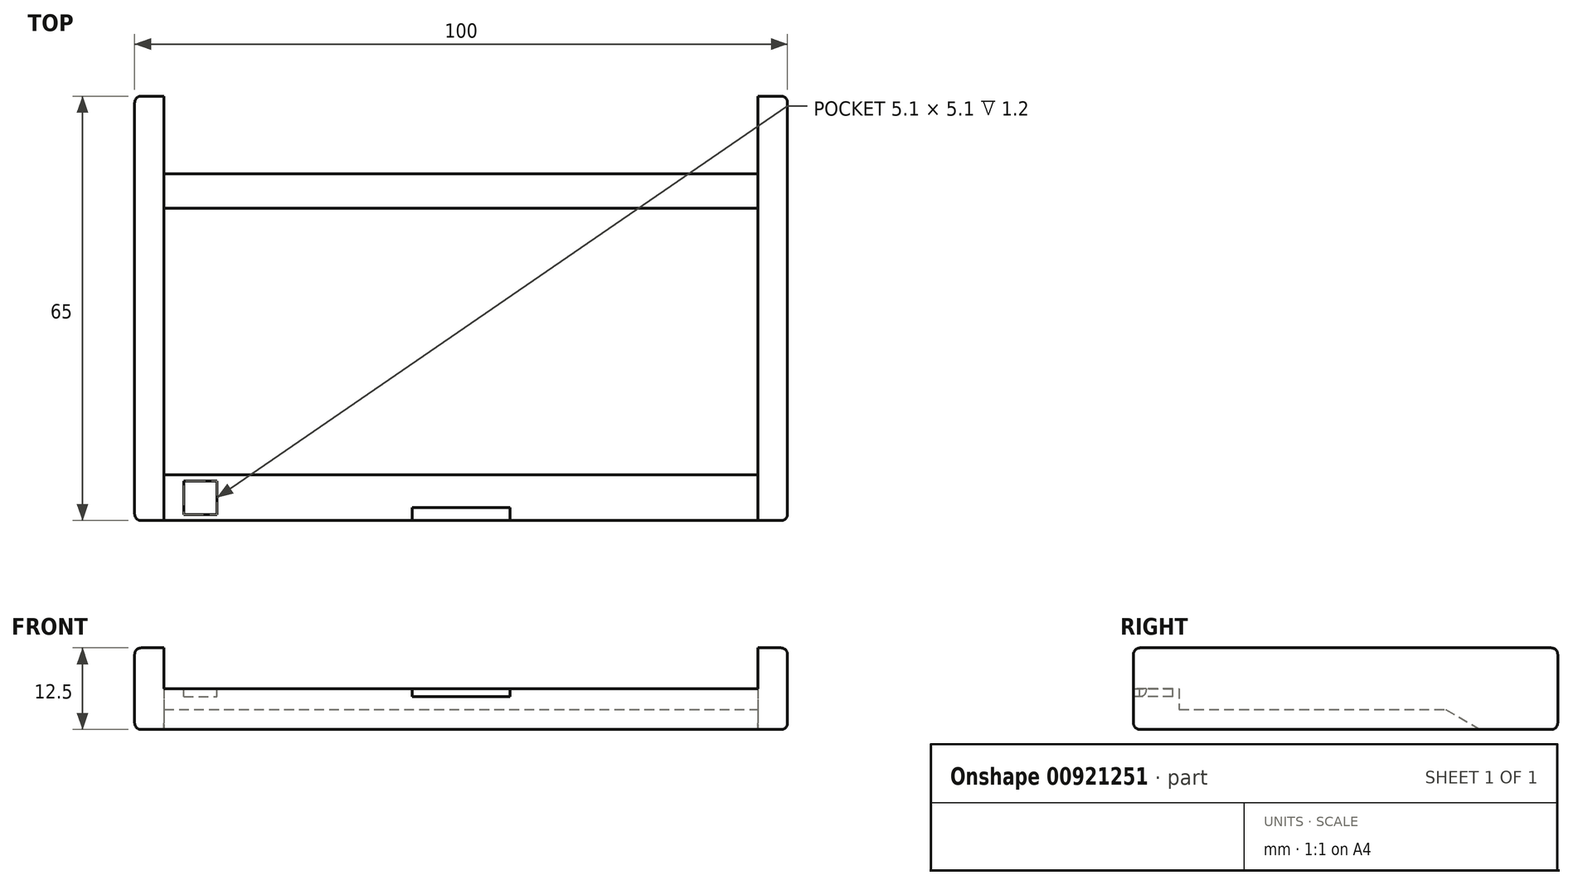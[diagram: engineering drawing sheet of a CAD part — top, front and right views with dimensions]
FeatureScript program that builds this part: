
annotation { "Feature Type Name" : "Feature", "Feature Type Description" : "" }
export const myFeature = defineFeature(function(context is Context, id is Id, definition is map)
    precondition{}
    {
        {
            var Q0;
            Q0=qCreatedBy(makeId("Right.planeOp"),FACE);
            var sketch = newSketch(context, id + "F0", { "sketchPlane" : qUnion([Q0])});
            skLineSegment(sketch, "E0.bottom", {"start": v(-32.5, 6.25) * mm, "end": v(32.5, 6.25) * mm});
            skLineSegment(sketch, "E0.top", {"start": v(-32.5, -6.25) * mm, "end": v(32.5, -6.25) * mm});
            skLineSegment(sketch, "E0.left", {"start": v(-32.5, 6.25) * mm, "end": v(-32.5, -6.25) * mm});
            skLineSegment(sketch, "E0.right", {"start": v(32.5, 6.25) * mm, "end": v(32.5, -6.25) * mm});
            skSolve(sketch);
        }
        {
            var Q0;
            Q0=makeQuery(id+"F0.imprint","IMPRINT",FACE,{"disambiguationData":[TD([[makeQuery(id+"F0.imprint","IMPRINT",EDGE,{"derivedFrom":sQuery(id+"F0.wireOp",EDGE,"E0.bottom")}),-1.0]])]});
            extrude(context, id + "F1", {"entities" : qUnion([Q0]), "endBound" : BoundingType.SYMMETRIC, "depth" : 100 * mm, "offsetDistance" : 25.4 * mm});
        }
        {
            var Q0;
            Q0=qCreatedBy(makeId("Right.planeOp"),FACE);
            var sketch = newSketch(context, id + "F2", { "sketchPlane" : qUnion([Q0])});
            skLineSegment(sketch, "E1", {"start": v(-32.5, 0) * mm, "end": v(-25.5, 0) * mm});
            skLineSegment(sketch, "E2", {"start": v(-25.5, 0) * mm, "end": v(-25.5, -3.2) * mm});
            skLineSegment(sketch, "E3", {"start": v(-25.5, -3.2) * mm, "end": v(15.33, -3.2) * mm});
            skLineSegment(sketch, "E4", {"start": v(15.33, -3.2) * mm, "end": v(20.62, -6.25) * mm});
            skLineSegment(sketch, "E5", {"start": v(-32.5, 0) * mm, "end": v(-32.5, 6.25) * mm});
            skLineSegment(sketch, "E6", {"start": v(-32.5, 6.25) * mm, "end": v(32.5, 6.25) * mm});
            skLineSegment(sketch, "E7", {"start": v(32.5, 6.25) * mm, "end": v(32.5, -6.25) * mm});
            skLineSegment(sketch, "E8", {"start": v(32.5, -6.25) * mm, "end": v(20.62, -6.25) * mm});
            skSolve(sketch);
        }
        {
            var Q0;
            Q0 = qSketchRegion(id + "F2", true);
            extrude(context, id + "F3", {"entities" : qUnion([Q0]), "operationType" : NewBodyOperationType.REMOVE, "endBound" : BoundingType.SYMMETRIC, "oppositeDirection" : true, "depth" : 91 * mm, "offsetDistance" : 25.4 * mm});
        }
        {
            var Q0;
            Q0=makeQuery(id+"F3.boolean.opBoolean","COPY",FACE,{"derivedFrom":makeQuery(id+"F3.opExtrude","SWEPT_FACE",FACE,{"disambiguationData":[OSD([sQuery(id+"F2.wireOp",EDGE,"E1")])]})});
            var sketch = newSketch(context, id + "F4", { "sketchPlane" : qUnion([Q0])});
            skLineSegment(sketch, "E9.bottom", {"start": v(-42.5, -26.47) * mm, "end": v(-37.4, -26.47) * mm});
            skLineSegment(sketch, "E9.top", {"start": v(-42.5, -31.57) * mm, "end": v(-37.4, -31.57) * mm});
            skLineSegment(sketch, "E9.left", {"start": v(-42.5, -26.47) * mm, "end": v(-42.5, -31.57) * mm});
            skLineSegment(sketch, "E9.right", {"start": v(-37.4, -26.47) * mm, "end": v(-37.4, -31.57) * mm});
            skSolve(sketch);
        }
        {
            var Q0;
            Q0 = qSketchRegion(id + "F4", true);
            extrude(context, id + "F5", {"entities" : qUnion([Q0]), "operationType" : NewBodyOperationType.REMOVE, "oppositeDirection" : true, "depth" : 1.2 * mm, "offsetDistance" : 25.4 * mm});
        }
        {
            var Q0;
            {var subQ0=sQuery(id+"F0.wireOp",EDGE,"E0.bottom");var subQ1=sQuery(id+"F0.wireOp",EDGE,"E0.left");Q0=makeQuery(id+"F3.boolean.opBoolean","SPLIT",EDGE,{"disambiguationData":[TD([makeQuery(id+"F1.opExtrude","CAP_FACE",FACE,{"disambiguationData":[OSD([subQ0,sQuery(id+"F0.wireOp",EDGE,"E0.top"),subQ1,sQuery(id+"F0.wireOp",EDGE,"E0.right")])],"isStart":true})])],"derivedFrom":makeQuery(id+"F1.opExtrude","SWEPT_EDGE",EDGE,{"disambiguationData":[OSD([subQ0,subQ1])]})});}
            var Q1;
            {var subQ0=sQuery(id+"F0.wireOp",EDGE,"E0.bottom");var subQ1=sQuery(id+"F0.wireOp",EDGE,"E0.left");Q1=makeQuery(id+"F3.boolean.opBoolean","SPLIT",EDGE,{"disambiguationData":[TD([makeQuery(id+"F1.opExtrude","CAP_FACE",FACE,{"disambiguationData":[OSD([subQ0,sQuery(id+"F0.wireOp",EDGE,"E0.top"),subQ1,sQuery(id+"F0.wireOp",EDGE,"E0.right")])],"isStart":false})])],"derivedFrom":makeQuery(id+"F1.opExtrude","SWEPT_EDGE",EDGE,{"disambiguationData":[OSD([subQ0,subQ1])]})});}
            var Q2;
            Q2=makeQuery(id+"F1.opExtrude","CAP_EDGE",EDGE,{"disambiguationData":[OSD([sQuery(id+"F0.wireOp",EDGE,"E0.bottom")])],"isStart":true});
            var Q3;
            {var subQ0=sQuery(id+"F0.wireOp",EDGE,"E0.bottom");var subQ1=sQuery(id+"F0.wireOp",EDGE,"E0.right");Q3=makeQuery(id+"F3.boolean.opBoolean","SPLIT",EDGE,{"disambiguationData":[TD([makeQuery(id+"F1.opExtrude","CAP_FACE",FACE,{"disambiguationData":[OSD([subQ0,sQuery(id+"F0.wireOp",EDGE,"E0.top"),sQuery(id+"F0.wireOp",EDGE,"E0.left"),subQ1])],"isStart":true})])],"derivedFrom":makeQuery(id+"F1.opExtrude","SWEPT_EDGE",EDGE,{"disambiguationData":[OSD([subQ0,subQ1])]})});}
            var Q4;
            {var subQ0=sQuery(id+"F0.wireOp",EDGE,"E0.bottom");var subQ1=sQuery(id+"F0.wireOp",EDGE,"E0.right");Q4=makeQuery(id+"F3.boolean.opBoolean","SPLIT",EDGE,{"disambiguationData":[TD([makeQuery(id+"F1.opExtrude","CAP_FACE",FACE,{"disambiguationData":[OSD([subQ0,sQuery(id+"F0.wireOp",EDGE,"E0.top"),sQuery(id+"F0.wireOp",EDGE,"E0.left"),subQ1])],"isStart":false})])],"derivedFrom":makeQuery(id+"F1.opExtrude","SWEPT_EDGE",EDGE,{"disambiguationData":[OSD([subQ0,subQ1])]})});}
            var Q5;
            Q5=makeQuery(id+"F1.opExtrude","CAP_EDGE",EDGE,{"disambiguationData":[OSD([sQuery(id+"F0.wireOp",EDGE,"E0.bottom")])],"isStart":false});
            var Q6;
            Q6=makeQuery(id+"F1.opExtrude","CAP_EDGE",EDGE,{"disambiguationData":[OSD([sQuery(id+"F0.wireOp",EDGE,"E0.left")])],"isStart":true});
            var Q7;
            Q7=makeQuery(id+"F1.opExtrude","CAP_EDGE",EDGE,{"disambiguationData":[OSD([sQuery(id+"F0.wireOp",EDGE,"E0.left")])],"isStart":false});
            var Q8;
            Q8=makeQuery(id+"F1.opExtrude","SWEPT_EDGE",EDGE,{"disambiguationData":[OSD([sQuery(id+"F0.wireOp",EDGE,"E0.top"),sQuery(id+"F0.wireOp",EDGE,"E0.left")])]});
            var Q9;
            Q9=makeQuery(id+"F1.opExtrude","CAP_EDGE",EDGE,{"disambiguationData":[OSD([sQuery(id+"F0.wireOp",EDGE,"E0.top")])],"isStart":false});
            var Q10;
            Q10=makeQuery(id+"F1.opExtrude","CAP_EDGE",EDGE,{"disambiguationData":[OSD([sQuery(id+"F0.wireOp",EDGE,"E0.right")])],"isStart":false});
            var Q11;
            Q11=makeQuery(id+"F1.opExtrude","CAP_EDGE",EDGE,{"disambiguationData":[OSD([sQuery(id+"F0.wireOp",EDGE,"E0.top")])],"isStart":true});
            var Q12;
            Q12=makeQuery(id+"F1.opExtrude","CAP_EDGE",EDGE,{"disambiguationData":[OSD([sQuery(id+"F0.wireOp",EDGE,"E0.right")])],"isStart":true});
            var Q13;
            {var subQ0=sQuery(id+"F0.wireOp",EDGE,"E0.right");var subQ1=sQuery(id+"F0.wireOp",EDGE,"E0.top");Q13=makeQuery(id+"F3.boolean.opBoolean","SPLIT",EDGE,{"disambiguationData":[TD([makeQuery(id+"F1.opExtrude","CAP_FACE",FACE,{"disambiguationData":[OSD([sQuery(id+"F0.wireOp",EDGE,"E0.bottom"),subQ1,sQuery(id+"F0.wireOp",EDGE,"E0.left"),subQ0])],"isStart":true})])],"derivedFrom":makeQuery(id+"F1.opExtrude","SWEPT_EDGE",EDGE,{"disambiguationData":[OSD([subQ1,subQ0])]})});}
            var Q14;
            {var subQ0=sQuery(id+"F0.wireOp",EDGE,"E0.right");var subQ1=sQuery(id+"F0.wireOp",EDGE,"E0.top");Q14=makeQuery(id+"F3.boolean.opBoolean","SPLIT",EDGE,{"disambiguationData":[TD([makeQuery(id+"F1.opExtrude","CAP_FACE",FACE,{"disambiguationData":[OSD([sQuery(id+"F0.wireOp",EDGE,"E0.bottom"),subQ1,sQuery(id+"F0.wireOp",EDGE,"E0.left"),subQ0])],"isStart":false})])],"derivedFrom":makeQuery(id+"F1.opExtrude","SWEPT_EDGE",EDGE,{"disambiguationData":[OSD([subQ1,subQ0])]})});}
            fillet(context, id + "F6", {"entities" : qUnion([Q0, Q1, Q2, Q3, Q4, Q5, Q6, Q7, Q8, Q9, Q10, Q11, Q12, Q13, Q14]), "radius" : 1 * mm, "tangentPropagation" : true, "allowEdgeOverflow" : false});
        }
        {
            var Q0;
            Q0=makeQuery(id+"F1.opExtrude","SWEPT_FACE",FACE,{"disambiguationData":[OSD([sQuery(id+"F0.wireOp",EDGE,"E0.left")])]});
            var sketch = newSketch(context, id + "F7", { "sketchPlane" : qUnion([Q0])});
            skLineSegment(sketch, "E10.bottom", {"start": v(-7.5, 0) * mm, "end": v(7.5, 0) * mm});
            skLineSegment(sketch, "E10.top", {"start": v(-7.5, -1.18) * mm, "end": v(7.5, -1.18) * mm});
            skLineSegment(sketch, "E10.left", {"start": v(-7.5, 0) * mm, "end": v(-7.5, -1.18) * mm});
            skLineSegment(sketch, "E10.right", {"start": v(7.5, 0) * mm, "end": v(7.5, -1.18) * mm});
            skSolve(sketch);
        }
        {
            var Q0;
            Q0=makeQuery(id+"F7.imprint","IMPRINT",FACE,{"disambiguationData":[TD([[makeQuery(id+"F7.imprint","IMPRINT",EDGE,{"derivedFrom":sQuery(id+"F7.wireOp",EDGE,"E10.bottom")}),-1.0]])]});
            extrude(context, id + "F8", {"entities" : qUnion([Q0]), "operationType" : NewBodyOperationType.REMOVE, "oppositeDirection" : true, "depth" : 2 * mm, "offsetDistance" : 25.4 * mm});
        }
        {
            var Q0;
            Q0=makeQuery(id+"F8.boolean.opBoolean","COPY",EDGE,{"derivedFrom":makeQuery(id+"F8.opExtrude","CAP_EDGE",EDGE,{"disambiguationData":[OSD([sQuery(id+"F7.wireOp",EDGE,"E10.top")])],"isStart":false})});
            fillet(context, id + "F9", {"entities" : qUnion([Q0]), "radius" : 1 * mm, "tangentPropagation" : true, "allowEdgeOverflow" : false});
        }
    });
